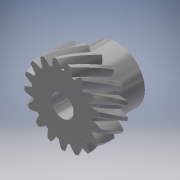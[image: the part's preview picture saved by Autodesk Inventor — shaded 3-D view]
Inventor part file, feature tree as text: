
AUTODESK INVENTOR PART (.ipt)
format: ipt  version: 2017 (Build 210142000, 142)  size: 483,328 bytes
history: native  units: mm (DEFAULTED — no unit token found)
features: extrude x4, sketch x4, plane x3, other x3
ambient origin geometry x8: Origin, YZ Plane, XZ Plane, XY Plane, X Axis, Y Axis, Z Axis, Center Point
bodies: Solid1 (feature_tree)
feature tree (14):
  extrude  "Extrusion1"  Depth=10.16mm TaperAngle=0.0deg
  plane  "Work Plane1"
  plane  "Work Plane2"
  plane  "Work Plane3"
  other  "Spur Gear"
  extrude  "Extrusion2"  Depth=76.2mm TaperAngle=0.0deg
  extrude  "Extrusion4"  TaperAngle=0.0deg  [1 undecoded]
  extrude  "Extrusion5"  TaperAngle=0.0deg  [1 undecoded]
  sketch  "Sketch1"  dims[d0=14.176796mm d1=10.16mm d2=0.0mm]
  sketch  "Sketch2"  dims[d3=12.552326mm d4=76.2mm d5=0.0mm]
  other  "Srf1"
  sketch  "Sketch5"  dims[d6=0.0mm d7=1.847996mm d9=0.0mm]
  sketch  "Sketch6"  dims[d14=0.0mm d15=31.75mm d16=0.0mm d17=0.0mm d18=0.0mm d19=31.75mm d21=25.4mm d22=0.0mm d28=3.048mm d30=10.16mm d31=0.0mm d32=2.54mm d33=10.16mm d34=15.24mm d35=5.08mm d36=0.0mm d37=4.064mm]
  other  "Pitch Diameter"
note: 2 required parameter values undecoded (feature->parameter linkage not recoverable at this tier; creation-order binding heuristic only, values carry confidence <= 0.55)
